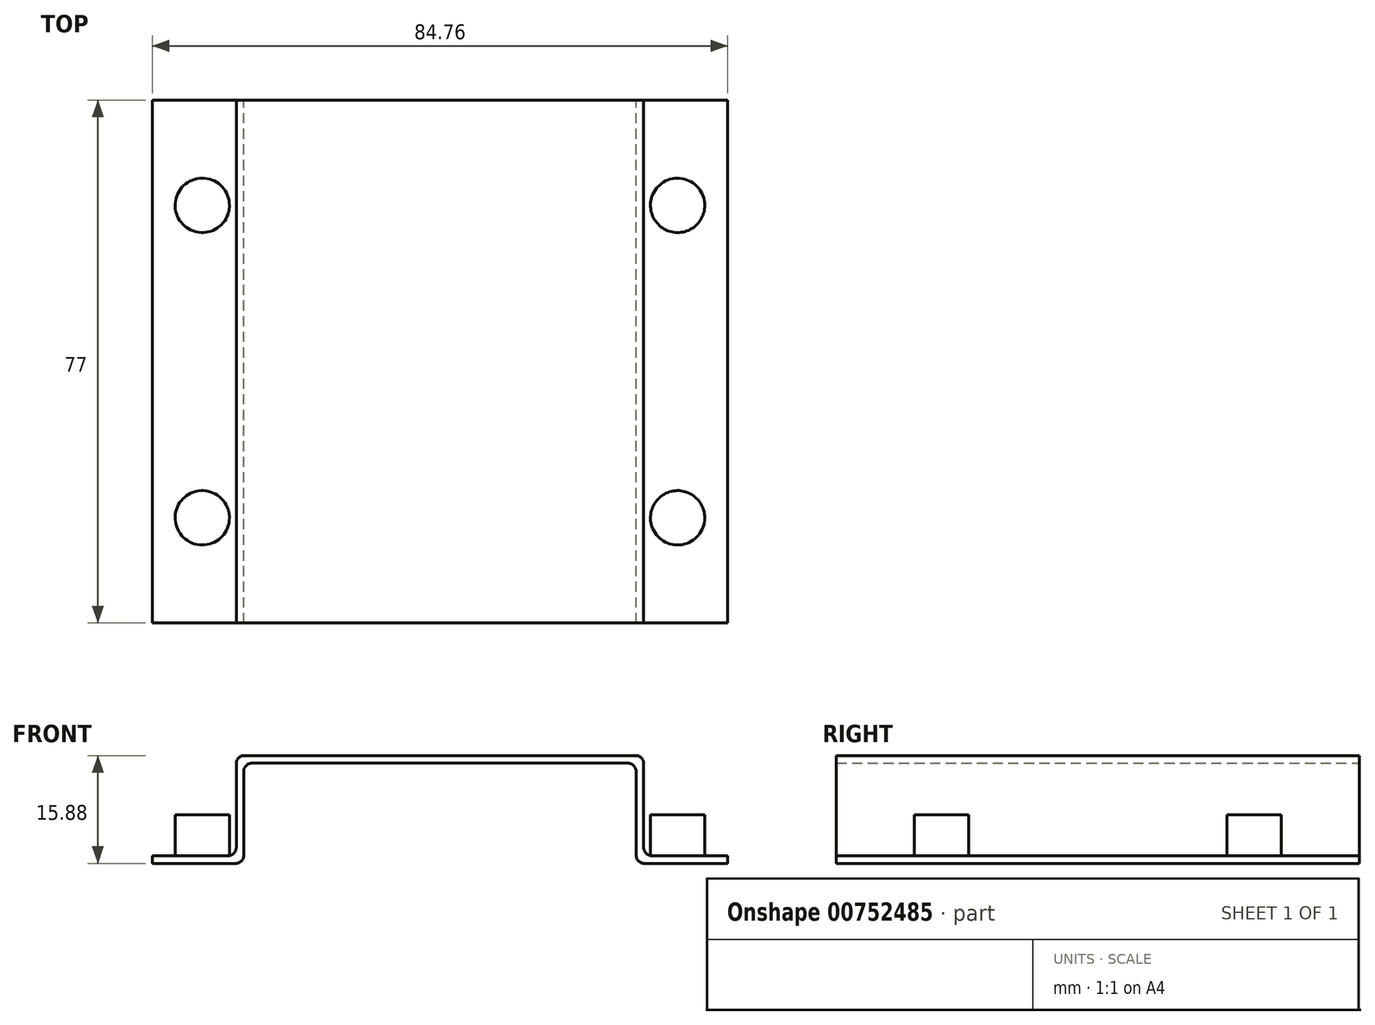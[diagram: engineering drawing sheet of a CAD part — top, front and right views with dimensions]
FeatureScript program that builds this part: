
annotation { "Feature Type Name" : "Feature", "Feature Type Description" : "" }
export const myFeature = defineFeature(function(context is Context, id is Id, definition is map)
    precondition{}
    {
        {
            var Q0;
            Q0=qCreatedBy(makeId("Front.planeOp"),FACE);
            var sketch = newSketch(context, id + "F0", { "sketchPlane" : qUnion([Q0])});
            skLineSegment(sketch, "E0", {"start": v(-42.38, 0) * mm, "end": v(-42.38, 1.12) * mm});
            skLineSegment(sketch, "E1", {"start": v(-42.38, 1.12) * mm, "end": v(-30, 1.12) * mm});
            skLineSegment(sketch, "E2", {"start": v(-30, 1.12) * mm, "end": v(-30, 15.88) * mm});
            skLineSegment(sketch, "E3", {"start": v(-30, 15.88) * mm, "end": v(30, 15.87) * mm});
            skLineSegment(sketch, "E4", {"start": v(30, 15.88) * mm, "end": v(30, 1.12) * mm});
            skLineSegment(sketch, "E5", {"start": v(30, 1.12) * mm, "end": v(42.38, 1.12) * mm});
            skLineSegment(sketch, "E6", {"start": v(42.38, 1.12) * mm, "end": v(42.38, 0) * mm});
            skLineSegment(sketch, "E7", {"start": v(42.38, 0) * mm, "end": v(28.88, 0) * mm});
            skLineSegment(sketch, "E8", {"start": v(28.88, 0) * mm, "end": v(28.88, 14.76) * mm});
            skLineSegment(sketch, "E9", {"start": v(28.88, 14.75) * mm, "end": v(-28.88, 14.75) * mm});
            skLineSegment(sketch, "E10", {"start": v(-28.88, 14.75) * mm, "end": v(-28.88, 0) * mm});
            skLineSegment(sketch, "E11", {"start": v(-28.88, 0) * mm, "end": v(-42.38, 0) * mm});
            skLineSegment(sketch, "E12", {"start": v(-28.88, 14.75) * mm, "end": v(-28.88, 15.88) * mm, "construction": true});
            skLineSegment(sketch, "E13", {"start": v(-30, 1.12) * mm, "end": v(-28.88, 1.12) * mm, "construction": true});
            skLineSegment(sketch, "E14", {"start": v(0, 14.75) * mm, "end": v(0, 0) * mm, "construction": true});
            skSolve(sketch);
        }
        {
            var Q0;
            Q0 = qSketchRegion(id + "F0", true);
            extrude(context, id + "F1", {"entities" : qUnion([Q0]), "depth" : 77 * mm, "offsetDistance" : 25 * mm});
        }
        {
            var Q0;
            Q0=makeQuery(id+"F1.opExtrude","SWEPT_EDGE",EDGE,{"disambiguationData":[OSD([sQuery(id+"F0.wireOp",EDGE,"E2"),sQuery(id+"F0.wireOp",EDGE,"E3")])]});
            var Q1;
            Q1=makeQuery(id+"F1.opExtrude","SWEPT_EDGE",EDGE,{"disambiguationData":[OSD([sQuery(id+"F0.wireOp",EDGE,"E3"),sQuery(id+"F0.wireOp",EDGE,"E4")])]});
            var Q2;
            Q2=makeQuery(id+"F1.opExtrude","SWEPT_EDGE",EDGE,{"disambiguationData":[OSD([sQuery(id+"F0.wireOp",EDGE,"E7"),sQuery(id+"F0.wireOp",EDGE,"E8")])]});
            var Q3;
            Q3=makeQuery(id+"F1.opExtrude","SWEPT_EDGE",EDGE,{"disambiguationData":[OSD([sQuery(id+"F0.wireOp",EDGE,"E10"),sQuery(id+"F0.wireOp",EDGE,"E11")])]});
            var Q4;
            Q4=makeQuery(id+"F1.opExtrude","SWEPT_EDGE",EDGE,{"disambiguationData":[OSD([sQuery(id+"F0.wireOp",EDGE,"E8"),sQuery(id+"F0.wireOp",EDGE,"E9")])]});
            var Q5;
            Q5=makeQuery(id+"F1.opExtrude","SWEPT_EDGE",EDGE,{"disambiguationData":[OSD([sQuery(id+"F0.wireOp",EDGE,"E9"),sQuery(id+"F0.wireOp",EDGE,"E10")])]});
            var Q6;
            Q6=makeQuery(id+"F1.opExtrude","SWEPT_EDGE",EDGE,{"disambiguationData":[OSD([sQuery(id+"F0.wireOp",EDGE,"E1"),sQuery(id+"F0.wireOp",EDGE,"E2")])]});
            var Q7;
            Q7=makeQuery(id+"F1.opExtrude","SWEPT_EDGE",EDGE,{"disambiguationData":[OSD([sQuery(id+"F0.wireOp",EDGE,"E4"),sQuery(id+"F0.wireOp",EDGE,"E5")])]});
            fillet(context, id + "F2", {"entities" : qUnion([Q0, Q1, Q2, Q3, Q4, Q5, Q6, Q7]), "radius" : 1.2 * mm, "tangentPropagation" : true, "allowEdgeOverflow" : false});
        }
        {
            var Q0;
            Q0=makeQuery(id+"F1.opExtrude","SWEPT_FACE",FACE,{"disambiguationData":[OSD([sQuery(id+"F0.wireOp",EDGE,"E5")])]});
            var sketch = newSketch(context, id + "F3", { "sketchPlane" : qUnion([Q0])});
            skCircle(sketch, "E15", {"center": v(35, -15.5) * mm, "radius": 4 * mm});
            skCircle(sketch, "E16", {"center": v(35, -61.5) * mm, "radius": 4 * mm});
            skLineSegment(sketch, "E17", {"start": v(35, -15.5) * mm, "end": v(35, -61.5) * mm, "construction": true});
            skLineSegment(sketch, "E18", {"start": v(35, -38.5) * mm, "end": v(42.38, -38.5) * mm, "construction": true});
            skCircle(sketch, "E19", {"center": v(-35, -15.5) * mm, "radius": 4 * mm});
            skCircle(sketch, "E20", {"center": v(-35, -61.5) * mm, "radius": 4 * mm});
            skLineSegment(sketch, "E21", {"start": v(-35, -15.5) * mm, "end": v(-35, -61.5) * mm, "construction": true});
            skLineSegment(sketch, "E22", {"start": v(-42.38, -38.5) * mm, "end": v(-35, -38.5) * mm, "construction": true});
            skSolve(sketch);
        }
        {
            var Q0;
            Q0 = qSketchRegion(id + "F3", true);
            extrude(context, id + "F4", {"entities" : qUnion([Q0]), "operationType" : NewBodyOperationType.ADD, "depth" : 6 * mm, "offsetDistance" : 25 * mm});
        }
    });
